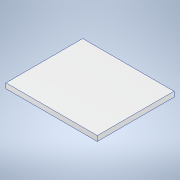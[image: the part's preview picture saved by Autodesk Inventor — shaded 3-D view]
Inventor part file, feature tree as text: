
AUTODESK INVENTOR PART (.ipt)
format: ipt  version: 2022 (Build 260153000, 153)  size: 92,672 bytes
history: native  units: mm
features: extrude x1, sketch x1
ambient origin geometry x8: Origin, YZ Plane, XZ Plane, XY Plane, X Axis, Y Axis, Z Axis, Center Point
bodies: Solid1 (feature_tree)
feature tree (2):
  extrude  "Extrusion1"  Depth=250.0mm
  sketch  "Sketch1"  dims[d0=210.0mm d1=250.0mm d2=14.0mm d3=0.0mm]
